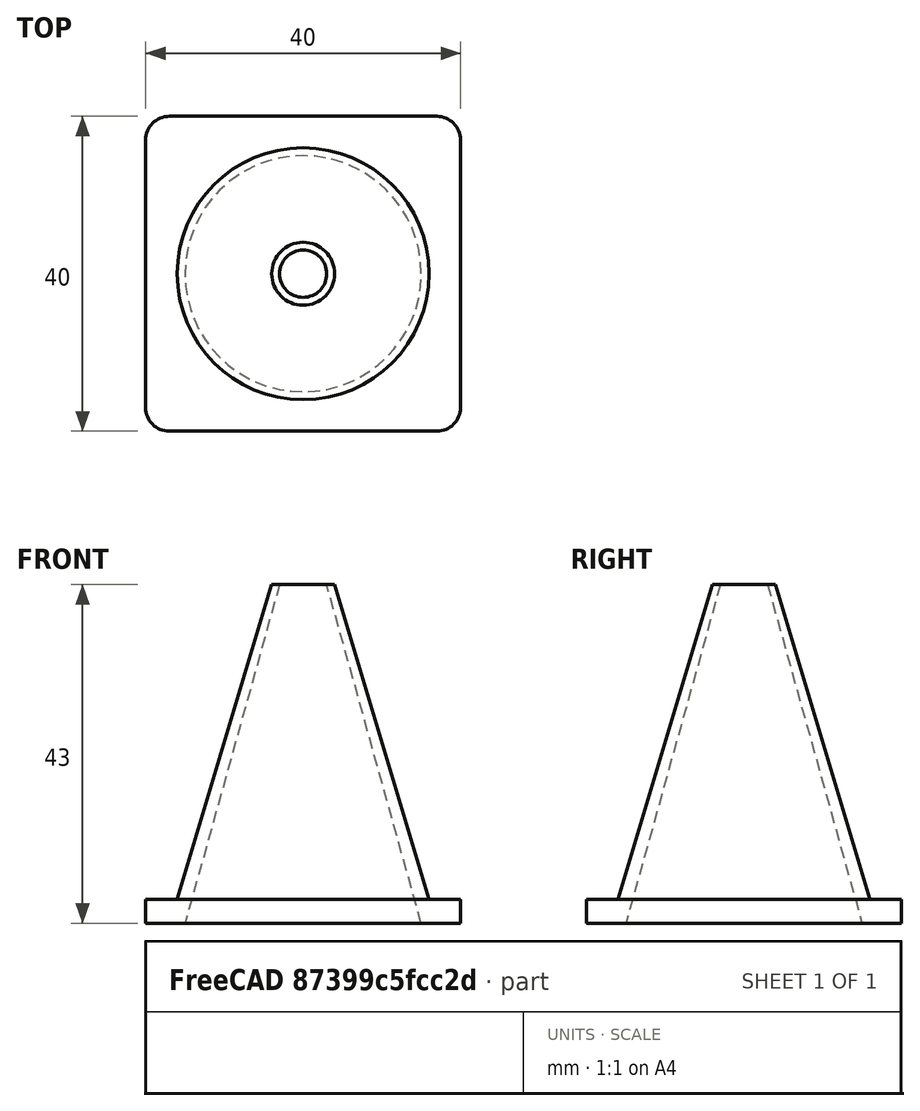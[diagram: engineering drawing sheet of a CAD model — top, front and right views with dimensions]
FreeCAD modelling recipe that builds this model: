
FCSTD DOCUMENT  (FreeCAD 0.16R6707 (Git))
Label: Cono
License: CreativeCommons Attribution-ShareAlike
LicenseURL: http://creativecommons.org/licenses/by-sa/4.0/
objects: Part::Cone×2, Part::Box×1, Part::MultiFuse×1, Part::Cut×1, Part::Fillet×1
note: 6 computed .brp shape members not serialized (recipe doc carries the construction recipe); baked Part::Feature solids carry a one-line shape summary decoded from their .brp

FEATURE [Part::Box] Box  label="Base"
  Height = 3
  Length = 40
  Width = 40
FEATURE [Part::Cone] Cone  label="Cono_ext"
  Angle = 360
  Height = 40
  Placement = pos=(20,20,3) rot=(0,0,1;0rad)
  Radius1 = 16
  Radius2 = 4
FEATURE [Part::Cone] Cone002  label="Cono_interior"
  Angle = 360
  Height = 43
  Placement = pos=(20,20,0) rot=(0,0,1;0rad)
  Radius1 = 15
  Radius2 = 3
FEATURE [Part::MultiFuse] Fusion  label="Cono_macizo"
  Shapes = -> [Box,Cone]
FEATURE [Part::Cut] Cut  label="Cono_Acabado"
  Base = -> Fusion
  Tool = -> Cone002
FEATURE [Part::Fillet] Fillet  label="Cono_redondeado"
  Base = -> Cut
  Edges = 4 edges r=3: [Edge1,Edge3,Edge6,Edge12]
